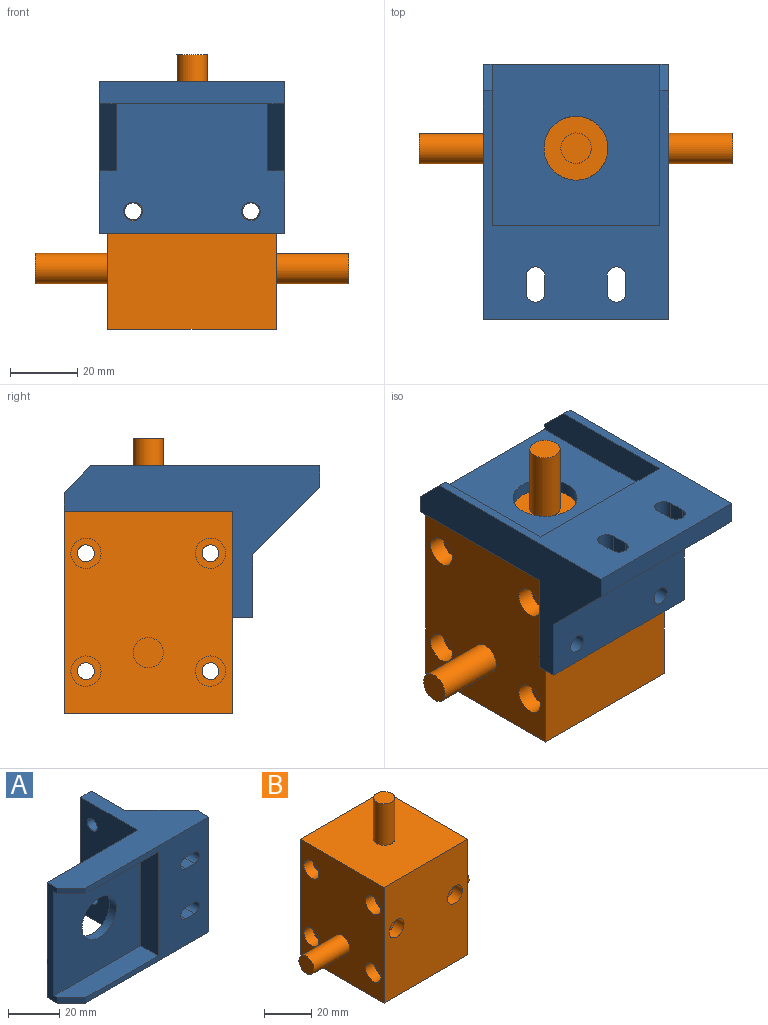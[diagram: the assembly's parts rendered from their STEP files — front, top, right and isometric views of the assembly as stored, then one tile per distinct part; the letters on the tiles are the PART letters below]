
ASSEMBLY  parts=2 mates=1
PART A: 31 faces, bbox 76x45x55 mm
  f0: plane 20x20mm, normal (0.71,0.71,0), area 141.4mm2, adj f8,f9,f11,f26
  f1: plane 55x5.5mm, normal (-1,0,0), area 217.8mm2, adj f2,f6,f7,f11,f12,f22,f23,f24
  f2: plane 8x8mm, normal (-0.71,-0.71,0), area 29.4mm2, adj f1,f3,f12,f23
  f3: plane 68x55mm, normal (0,-1,0), area 1645.5mm2, adj f2,f7,f8,f11,f12,f13,f14,f15
  f4: plane 20x20mm, normal (0.71,0.71,0), area 141.4mm2, adj f8,f9,f12,f27
  f5: plane 55x31.5mm, normal (-1,0,0), area 1685mm2, adj f6,f10,f11,f12,f29,f30
  f6: plane 55x50mm, normal (0,1,0), area 2466.5mm2, adj f1,f5,f11,f12,f21
  f7: plane 8x8mm, normal (-0.71,-0.71,0), area 29.4mm2, adj f1,f3,f11,f24
  f8: plane 55x6.5mm, normal (1,0,0), area 357.5mm2, adj f0,f3,f4,f11,f12,f28
  f9: plane 55x38.5mm, normal (1,0,0), area 1870mm2, adj f0,f4,f10,f11,f12,f26,f27,f28
  f10: plane 55x6mm, normal (0,1,0), area 330mm2, adj f5,f9,f11,f12
  f11: plane 76x45mm, normal (0,0,1), area 1243mm2, adj f0,f1,f3,f5,f6,f7,f8,f9
  f12: plane 76x45mm, normal (0,0,-1), area 1243mm2, adj f1,f2,f3,f4,f5,f6,f8,f9
  f13: cylinder r=2.75mm len=6.5mm, axis (0,-1,0), area 56.2mm2, adj f3,f14,f16,f28
  f14: plane 6.5x5mm, normal (0,0,1), area 32.5mm2, adj f3,f13,f15,f28
  f15: cylinder r=2.75mm len=6.5mm, axis (0,-1,0), area 56.2mm2, adj f3,f14,f16,f28
  f16: plane 6.5x5mm, normal (0,0,-1), area 32.5mm2, adj f3,f13,f15,f28
  f17: cylinder r=2.75mm len=6.5mm, axis (0,-1,0), area 56.2mm2, adj f3,f18,f20,f28
  f18: plane 6.5x5mm, normal (0,0,1), area 32.5mm2, adj f3,f17,f19,f28
  f19: cylinder r=2.75mm len=6.5mm, axis (0,-1,0), area 56.2mm2, adj f3,f18,f20,f28
  f20: plane 6.5x5mm, normal (0,0,-1), area 32.5mm2, adj f3,f17,f19,f28
  f21: cylinder r=9.5mm len=19mm, axis (0,-1,0), area 226.8mm2, adj f6,f22
  f22: plane 49.8x48mm, normal (0,-1,0), area 2106.9mm2, adj f1,f21,f23,f24,f25
  f23: plane 48x9.7mm, normal (0,0,1), area 433.6mm2, adj f1,f2,f3,f22,f25
  f24: plane 48x9.7mm, normal (0,0,-1), area 433.6mm2, adj f1,f3,f7,f22,f25
  f25: plane 49.8x9.7mm, normal (-1,0,0), area 483.1mm2, adj f3,f22,f23,f24
  f26: plane 20x20mm, normal (0,0,-1), area 200mm2, adj f0,f9,f28
  f27: plane 20x20mm, normal (0,0,1), area 200mm2, adj f4,f9,f28
  f28: plane 45x20mm, normal (0,1,0), area 797.5mm2, adj f8,f9,f13,f14,f15,f16,f17,f18
  f29: cylinder r=2.75mm len=6mm, axis (1,0,0), area 103.7mm2, adj f5,f9
  f30: cylinder r=2.75mm len=6mm, axis (1,0,0), area 103.7mm2, adj f5,f9
PART B: 42 faces, bbox 93x50x81.5 mm
  f0: cylinder r=2.5mm len=39.5mm, axis (0,1,0), area 620.5mm2, adj f37,f40
  f1: cylinder r=2.5mm len=39.5mm, axis (0,1,0), area 620.5mm2, adj f35,f38
  f2: plane 60x50mm, normal (-1,0,0), area 2681.9mm2, adj f3,f5,f6,f7,f16,f18,f20,f22
  f3: plane 60x50mm, normal (0,-1,0), area 2872.8mm2, adj f2,f4,f6,f7,f39,f41
  f4: plane 60x50mm, normal (1,0,0), area 2681.9mm2, adj f3,f5,f6,f7,f8,f10,f12,f14
  f5: plane 60x50mm, normal (0,1,0), area 2872.8mm2, adj f2,f4,f6,f7,f34,f36
  f6: plane 50x50mm, normal (0,0,1), area 2436.4mm2, adj f2,f3,f4,f5,f32
  f7: plane 50x50mm, normal (0,0,-1), area 2500mm2, adj f2,f3,f4,f5
  f8: cylinder r=4.5mm len=9mm, axis (1,0,0), area 148.4mm2, adj f4,f9
  f9: plane 9x9mm, normal (1,0,0), area 44mm2, adj f8,f27
  f10: cylinder r=4.5mm len=9mm, axis (1,0,0), area 148.4mm2, adj f4,f11
  f11: plane 9x9mm, normal (1,0,0), area 44mm2, adj f10,f25
  f12: cylinder r=4.5mm len=9mm, axis (1,0,0), area 148.4mm2, adj f4,f13
  f13: plane 9x9mm, normal (1,0,0), area 44mm2, adj f12,f26
  f14: cylinder r=4.5mm len=9mm, axis (1,0,0), area 148.4mm2, adj f4,f15
  f15: plane 9x9mm, normal (1,0,0), area 44mm2, adj f14,f24
  f16: cylinder r=4.5mm len=9mm, axis (-1,0,0), area 148.4mm2, adj f2,f17
  f17: plane 9x9mm, normal (-1,0,0), area 44mm2, adj f16,f27
  f18: cylinder r=4.5mm len=9mm, axis (-1,0,0), area 148.4mm2, adj f2,f19
  f19: plane 9x9mm, normal (-1,0,0), area 44mm2, adj f18,f26
  f20: cylinder r=4.5mm len=9mm, axis (-1,0,0), area 148.4mm2, adj f2,f21
  f21: plane 9x9mm, normal (-1,0,0), area 44mm2, adj f20,f25
  f22: cylinder r=4.5mm len=9mm, axis (-1,0,0), area 148.4mm2, adj f2,f23
  f23: plane 9x9mm, normal (-1,0,0), area 44mm2, adj f22,f24
  f24: cylinder r=2.5mm len=39.5mm, axis (-1,0,0), area 620.5mm2, adj f15,f23
  f25: cylinder r=2.5mm len=39.5mm, axis (-1,0,0), area 620.5mm2, adj f11,f21
  f26: cylinder r=2.5mm len=39.5mm, axis (-1,0,0), area 620.5mm2, adj f13,f19
  f27: cylinder r=2.5mm len=39.5mm, axis (-1,0,0), area 620.5mm2, adj f9,f17
  f28: cylinder r=4.5mm len=21.5mm, axis (1,0,0), area 607.9mm2, adj f2,f29
  f29: plane 9x9mm, normal (-1,0,0), area 63.6mm2, adj f28
  f30: cylinder r=4.5mm len=21.5mm, axis (-1,0,0), area 607.9mm2, adj f4,f31
  f31: plane 9x9mm, normal (1,0,0), area 63.6mm2, adj f30
  f32: cylinder r=4.5mm len=21.5mm, axis (0,0,-1), area 607.9mm2, adj f6,f33
  f33: plane 9x9mm, normal (0,0,1), area 63.6mm2, adj f32
  f34: cylinder r=4.5mm len=9mm, axis (0,1,0), area 148.4mm2, adj f5,f35
  f35: plane 9x9mm, normal (0,1,0), area 44mm2, adj f1,f34
  f36: cylinder r=4.5mm len=9mm, axis (0,1,0), area 148.4mm2, adj f5,f37
  f37: plane 9x9mm, normal (0,1,0), area 44mm2, adj f0,f36
  f38: plane 9x9mm, normal (0,-1,0), area 44mm2, adj f1,f39
  f39: cylinder r=4.5mm len=9mm, axis (0,-1,0), area 148.4mm2, adj f3,f38
  f40: plane 9x9mm, normal (0,-1,0), area 44mm2, adj f0,f41
  f41: cylinder r=4.5mm len=9mm, axis (0,-1,0), area 148.4mm2, adj f3,f40
PLACE A rot(axis=(-0.58,0.58,-0.58),120deg) t=(-150.82,-196.02,139.99)mm
PLACE B t=(-86.86,-19.76,36.58)mm
MATE fastened A.f21 <-> B.f32  axis (0,0,-1) through (-123.32,-8.59,96.58)mm
